annotation { "Feature Type Name" : "Feature", "Feature Type Description" : "" }
export const myFeature = defineFeature(function(context is Context, id is Id, definition is map)
    precondition{}
    {
        {
            var Q0;
            Q0=qCreatedBy(makeId("Front.planeOp"),FACE);
            var sketch = newSketch(context, id + "F0", { "sketchPlane" : qUnion([Q0])});
            skLineSegment(sketch, "E0", {"start": v(-13, 11.3) * mm, "end": v(-13, 17.18) * mm});
            skLineSegment(sketch, "E1", {"start": v(-13, 17.18) * mm, "end": v(-6.8, 21.51) * mm});
            skLineSegment(sketch, "E2", {"start": v(-6.8, 21.51) * mm, "end": v(0, 17.18) * mm});
            skLineSegment(sketch, "E3", {"start": v(0, 17.18) * mm, "end": v(5.57, 21.51) * mm});
            skLineSegment(sketch, "E4", {"start": v(5.57, 21.51) * mm, "end": v(11.45, 17.18) * mm});
            skLineSegment(sketch, "E5", {"start": v(11.45, 17.18) * mm, "end": v(11.45, 10.99) * mm});
            skLineSegment(sketch, "E6", {"start": v(11.45, 10.99) * mm, "end": v(17.95, 7.58) * mm});
            skLineSegment(sketch, "E7", {"start": v(17.95, 7.58) * mm, "end": v(17.95, -6.04) * mm});
            skLineSegment(sketch, "E8", {"start": v(17.95, -6.04) * mm, "end": v(11.45, -10.06) * mm});
            skLineSegment(sketch, "E9", {"start": v(11.45, -10.06) * mm, "end": v(11.45, -15.94) * mm});
            skLineSegment(sketch, "E10", {"start": v(11.45, -15.94) * mm, "end": v(5.57, -20.58) * mm});
            skLineSegment(sketch, "E11", {"start": v(5.57, -20.58) * mm, "end": v(0, -15.94) * mm});
            skLineSegment(sketch, "E12", {"start": v(0, -15.94) * mm, "end": v(-6.8, -20.58) * mm});
            skLineSegment(sketch, "E13", {"start": v(-6.8, -20.58) * mm, "end": v(-13, -15.94) * mm});
            skLineSegment(sketch, "E14", {"start": v(-13, 11.3) * mm, "end": v(-18.26, 7.9) * mm});
            skLineSegment(sketch, "E15", {"start": v(-18.26, 7.9) * mm, "end": v(-18.26, -5.73) * mm});
            skLineSegment(sketch, "E16", {"start": v(-18.26, -5.73) * mm, "end": v(-13, -9.75) * mm});
            skLineSegment(sketch, "E17", {"start": v(-13, -9.75) * mm, "end": v(-13, -15.94) * mm});
            skLineSegment(sketch, "E18.bottom", {"start": v(-43.64, 38.53) * mm, "end": v(48.9, 38.53) * mm});
            skLineSegment(sketch, "E18.top", {"start": v(-43.64, -53.7) * mm, "end": v(48.9, -53.7) * mm});
            skLineSegment(sketch, "E18.left", {"start": v(-43.64, 38.53) * mm, "end": v(-43.64, -53.7) * mm});
            skLineSegment(sketch, "E18.right", {"start": v(48.9, 38.53) * mm, "end": v(48.9, -53.7) * mm});
            skPoint(sketch, "E19.0.midPoint", {"position": v(-35.65, 25.22) * mm});
            skLineSegment(sketch, "E20", {"start": v(-35.65, 36.99) * mm, "end": v(-34.2, 32.5) * mm});
            skLineSegment(sketch, "E21", {"start": v(-41.84, 32.5) * mm, "end": v(-37.11, 32.5) * mm});
            skLineSegment(sketch, "E22", {"start": v(-39.48, 25.22) * mm, "end": v(-38.02, 29.72) * mm});
            skLineSegment(sketch, "E23", {"start": v(-41.84, 32.5) * mm, "end": v(-38.02, 29.72) * mm});
            skLineSegment(sketch, "E24", {"start": v(-29.47, 32.5) * mm, "end": v(-33.3, 29.72) * mm});
            skLineSegment(sketch, "E25.trimOffspring", {"start": v(-33.3, 29.72) * mm, "end": v(-31.83, 25.22) * mm});
            skLineSegment(sketch, "E26.trimOffspring", {"start": v(-34.2, 32.5) * mm, "end": v(-29.47, 32.5) * mm});
            skLineSegment(sketch, "E27.trimOffspring", {"start": v(-37.11, 32.5) * mm, "end": v(-35.65, 36.99) * mm});
            skLineSegment(sketch, "E28.trimOffspring", {"start": v(-35.65, 28) * mm, "end": v(-31.83, 25.22) * mm});
            skLineSegment(sketch, "E29.trimOffspring", {"start": v(-35.65, 28) * mm, "end": v(-39.48, 25.22) * mm});
            skLineSegment(sketch, "E30", {"start": v(-6.99, 13.76) * mm, "end": v(-6.99, 7.32) * mm});
            skLineSegment(sketch, "E31", {"start": v(-6.99, 7.32) * mm, "end": v(-18.26, 1.08) * mm});
            skLineSegment(sketch, "E32", {"start": v(-18.26, 1.08) * mm, "end": v(-6.99, -5.16) * mm});
            skLineSegment(sketch, "E33", {"start": v(-6.99, -5.16) * mm, "end": v(-6.99, -12.37) * mm});
            skLineSegment(sketch, "E34", {"start": v(5.77, 14.19) * mm, "end": v(5.77, 7.32) * mm});
            skLineSegment(sketch, "E35", {"start": v(5.77, 7.32) * mm, "end": v(16.8, 0.77) * mm});
            skPoint(sketch, "E35.endSnap0", {"position": v(17.95, 0.77) * mm});
            skLineSegment(sketch, "E36", {"start": v(16.8, 0.77) * mm, "end": v(5.77, -5.97) * mm});
            skLineSegment(sketch, "E37", {"start": v(5.77, -5.97) * mm, "end": v(5.77, -12.37) * mm});
            skLineSegment(sketch, "E38", {"start": v(5.77, -12.37) * mm, "end": v(0, -9.37) * mm});
            skLineSegment(sketch, "E39", {"start": v(0, -9.37) * mm, "end": v(-6.29, -12.37) * mm});
            skLineSegment(sketch, "E40", {"start": v(-6.99, 13.76) * mm, "end": v(-0.51, 9.91) * mm});
            skLineSegment(sketch, "E41", {"start": v(-0.51, 9.91) * mm, "end": v(5.77, 14.19) * mm});
            skCircle(sketch, "E42", {"center": v(0, 0) * mm, "radius": 7.4 * mm});
            skCircle(sketch, "E43", {"center": v(0, 0) * mm, "radius": 6 * mm});
            skCircle(sketch, "E44", {"center": v(0, 0) * mm, "radius": 4.78 * mm});
            skCircle(sketch, "E45", {"center": v(0, 0) * mm, "radius": 3.55 * mm});
            skCircle(sketch, "E46", {"center": v(0, 0) * mm, "radius": 2.66 * mm});
            skLineSegment(sketch, "E47.bottom", {"start": v(-43.64, 38.53) * mm, "end": v(0, 38.53) * mm});
            skLineSegment(sketch, "E47.top", {"start": v(-43.64, 0) * mm, "end": v(0, 0) * mm});
            skLineSegment(sketch, "E47.left", {"start": v(-43.64, 38.53) * mm, "end": v(-43.64, 0) * mm});
            skLineSegment(sketch, "E47.right", {"start": v(0, 38.53) * mm, "end": v(0, 0) * mm});
            skLineSegment(sketch, "E48.bottom", {"start": v(48.9, 38.53) * mm, "end": v(0, 38.53) * mm});
            skLineSegment(sketch, "E48.top", {"start": v(48.9, 0) * mm, "end": v(0, 0) * mm});
            skLineSegment(sketch, "E48.left", {"start": v(48.9, 38.53) * mm, "end": v(48.9, 0) * mm});
            skLineSegment(sketch, "E49.bottom", {"start": v(0, 0) * mm, "end": v(48.9, 0) * mm});
            skLineSegment(sketch, "E49.top", {"start": v(0, -53.7) * mm, "end": v(48.9, -53.7) * mm});
            skLineSegment(sketch, "E49.left", {"start": v(0, 0) * mm, "end": v(0, -53.7) * mm});
            skLineSegment(sketch, "E49.right", {"start": v(48.9, 0) * mm, "end": v(48.9, -53.7) * mm});
            skSolve(sketch);
        }
        {
            var Q0;
            Q0 = qSketchRegion(id + "F0", true);
            extrude(context, id + "F1", {"entities" : qUnion([Q0]), "depth" : 12.7 * mm});
        }
        {
            var Q0;
            Q0=makeQuery(id+"F1.opExtrude","CAP_FACE",FACE,{"disambiguationData":[OSD([sQuery(id+"F0.wireOp",EDGE,"E0"),sQuery(id+"F0.wireOp",EDGE,"E1"),sQuery(id+"F0.wireOp",EDGE,"E2"),sQuery(id+"F0.wireOp",EDGE,"E3"),sQuery(id+"F0.wireOp",EDGE,"E4"),sQuery(id+"F0.wireOp",EDGE,"E5"),sQuery(id+"F0.wireOp",EDGE,"E6"),sQuery(id+"F0.wireOp",EDGE,"E7"),sQuery(id+"F0.wireOp",EDGE,"E8"),sQuery(id+"F0.wireOp",EDGE,"E9"),sQuery(id+"F0.wireOp",EDGE,"E10"),sQuery(id+"F0.wireOp",EDGE,"E11"),sQuery(id+"F0.wireOp",EDGE,"E12"),sQuery(id+"F0.wireOp",EDGE,"E13"),sQuery(id+"F0.wireOp",EDGE,"E14"),sQuery(id+"F0.wireOp",EDGE,"E15"),sQuery(id+"F0.wireOp",EDGE,"E16"),sQuery(id+"F0.wireOp",EDGE,"E17"),sQuery(id+"F0.wireOp",EDGE,"E18.top"),sQuery(id+"F0.wireOp",EDGE,"E18.left"),sQuery(id+"F0.wireOp",EDGE,"E20"),sQuery(id+"F0.wireOp",EDGE,"E21"),sQuery(id+"F0.wireOp",EDGE,"E22"),sQuery(id+"F0.wireOp",EDGE,"E23"),sQuery(id+"F0.wireOp",EDGE,"E24"),sQuery(id+"F0.wireOp",EDGE,"E25.trimOffspring"),sQuery(id+"F0.wireOp",EDGE,"E26.trimOffspring"),sQuery(id+"F0.wireOp",EDGE,"E27.trimOffspring"),sQuery(id+"F0.wireOp",EDGE,"E28.trimOffspring"),sQuery(id+"F0.wireOp",EDGE,"E29.trimOffspring"),sQuery(id+"F0.wireOp",EDGE,"E47.bottom"),sQuery(id+"F0.wireOp",EDGE,"E47.left"),sQuery(id+"F0.wireOp",EDGE,"E48.bottom"),sQuery(id+"F0.wireOp",EDGE,"E48.left"),sQuery(id+"F0.wireOp",EDGE,"E49.top"),sQuery(id+"F0.wireOp",EDGE,"E49.right")])],"isStart":false});
            var sketch = newSketch(context, id + "F2", { "sketchPlane" : qUnion([Q0])});
            skText(sketch, "E50", { "text": "Mya Pugh", "fontName": "OpenSans-Bold.ttf"});
            const initialGuessF2  = {"E50": [-0.04168, -0.04143, 1, 0, 0.01314]};
            skSetInitialGuess(sketch, initialGuessF2);
            skSolve(sketch);
        }
        {
            var Q0;
            Q0 = qSketchRegion(id + "F2", true);
            extrude(context, id + "F3", {"entities" : qUnion([Q0]), "operationType" : NewBodyOperationType.REMOVE, "oppositeDirection" : true, "depth" : 25.4 * mm});
        }
    });